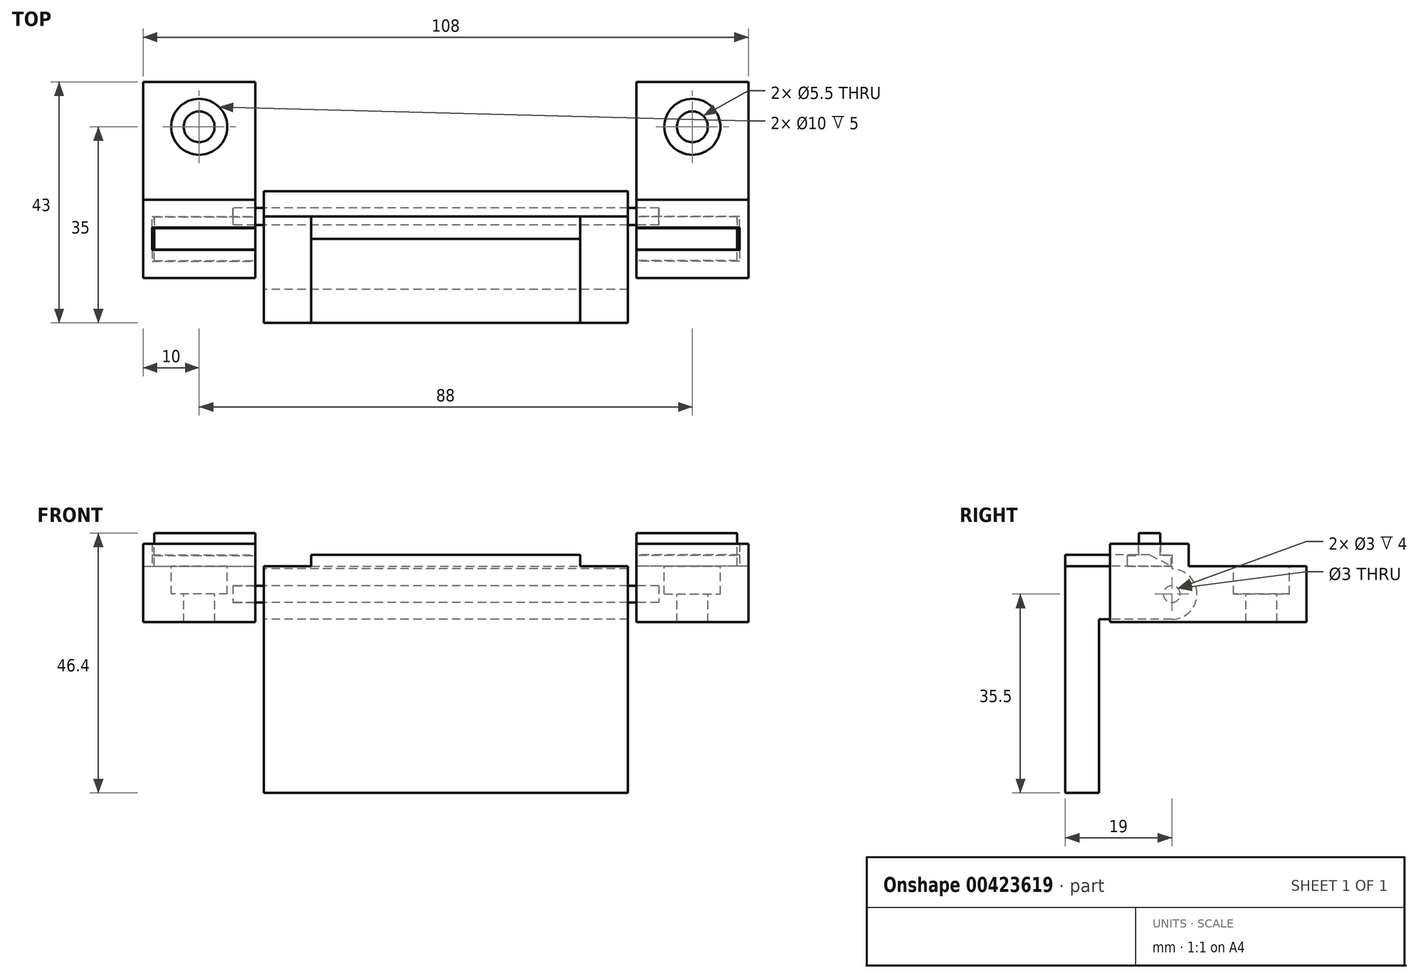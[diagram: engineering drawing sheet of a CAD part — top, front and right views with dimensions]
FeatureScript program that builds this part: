
annotation { "Feature Type Name" : "Feature", "Feature Type Description" : "" }
export const myFeature = defineFeature(function(context is Context, id is Id, definition is map)
    precondition{}
    {
        {
            var Q0;
            Q0=qCreatedBy(makeId("Top.planeOp"),FACE);
            var sketch = newSketch(context, id + "F0", { "sketchPlane" : qUnion([Q0])});
            skLineSegment(sketch, "E0.bottom", {"start": v(-54, 0) * mm, "end": v(-34, 0) * mm});
            skLineSegment(sketch, "E0.top", {"start": v(-54, 35) * mm, "end": v(-34, 35) * mm});
            skLineSegment(sketch, "E0.left", {"start": v(-54, 0) * mm, "end": v(-54, 35) * mm});
            skLineSegment(sketch, "E0.right", {"start": v(-34, 0) * mm, "end": v(-34, 35) * mm});
            skLineSegment(sketch, "E1", {"start": v(-44, 35) * mm, "end": v(-44, 0) * mm, "construction": true});
            skSolve(sketch);
        }
        {
            var Q0;
            Q0=makeQuery(id+"F0.imprint","IMPRINT",FACE,{"disambiguationData":[TD([[makeQuery(id+"F0.imprint","IMPRINT",EDGE,{"derivedFrom":sQuery(id+"F0.wireOp",EDGE,"E0.bottom")}),1.0]])]});
            var Q1;
            Q1=makeQuery(id+"F0.imprint","IMPRINT",FACE,{"disambiguationData":[TD([[makeQuery(id+"F0.imprint","IMPRINT",EDGE,{"derivedFrom":sQuery(id+"F0.wireOp",EDGE,"f8b40c92-a36b-450e-9c67-8d930c3af6210.MirrorCS")}),-1.0]])]});
            extrude(context, id + "F1", {"entities" : qUnion([Q0, Q1]), "depth" : 10 * mm});
        }
        {
            var Q0;
            Q0=makeQuery(id+"F1.opExtrude","CAP_FACE",FACE,{"disambiguationData":[OSD([sQuery(id+"F0.wireOp",EDGE,"E0.bottom"),sQuery(id+"F0.wireOp",EDGE,"E0.top"),sQuery(id+"F0.wireOp",EDGE,"E0.left"),sQuery(id+"F0.wireOp",EDGE,"E0.right")])],"isStart":false});
            var sketch = newSketch(context, id + "F2", { "sketchPlane" : qUnion([Q0])});
            skPoint(sketch, "E2", {"position": v(-44, 27) * mm});
            skLineSegment(sketch, "E3", {"start": v(-44, 35) * mm, "end": v(-44, 0) * mm, "construction": true});
            skLineSegment(sketch, "E4", {"start": v(-54, 17.5) * mm, "end": v(-34, 17.5) * mm, "construction": true});
            skSolve(sketch);
        }
        {
            var Q0;
            Q0=sQuery(id+"F2.wireOp",VERTEX,"E2");
            var Q1;
            Q1=makeQuery(id+"F1.opExtrude","SWEPT_BODY",BODY,{"disambiguationData":[OSD([sQuery(id+"F0.wireOp",EDGE,"E0.bottom"),sQuery(id+"F0.wireOp",EDGE,"E0.top"),sQuery(id+"F0.wireOp",EDGE,"E0.left"),sQuery(id+"F0.wireOp",EDGE,"E0.right")])]});
            hole(context, id + "F3", {"style" : HoleStyle.C_BORE, "endStyle" : HoleEndStyle.THROUGH, "holeDiameter" : 5.5 * mm, "cBoreDiameter" : 10 * mm, "cBoreDepth" : 5 * mm, "isTappedThrough" : true, "tappedDepth" : 3 * mm, "tapClearance" : 3, "locations" : qUnion([Q0]), "scope" : qUnion([Q1])});
        }
        {
            var Q0;
            Q0=makeQuery(id+"F1.opExtrude","SWEPT_FACE",FACE,{"disambiguationData":[OSD([sQuery(id+"F0.wireOp",EDGE,"E0.right")])]});
            var sketch = newSketch(context, id + "F4", { "sketchPlane" : qUnion([Q0])});
            skPoint(sketch, "E5", {"position": v(11, 5) * mm});
            skLineSegment(sketch, "E6", {"start": v(0, 5) * mm, "end": v(35, 5) * mm, "construction": true});
            skCircle(sketch, "E7", {"center": v(11, 5) * mm, "radius": 1.5 * mm});
            skLineSegment(sketch, "E8.0", {"start": v(22, 10) * mm, "end": v(32, 10) * mm, "construction": true});
            skLineSegment(sketch, "E9", {"start": v(22, 10) * mm, "end": v(22, 0) * mm, "construction": true});
            skPoint(sketch, "E10", {"position": v(22, 5) * mm});
            skLineSegment(sketch, "E11", {"start": v(11, 3.5) * mm, "end": v(11, 6.5) * mm, "construction": true});
            skLineSegment(sketch, "E12", {"start": v(0, 10) * mm, "end": v(0, 14) * mm});
            skLineSegment(sketch, "E13", {"start": v(0, 14) * mm, "end": v(5, 14) * mm});
            skLineSegment(sketch, "E14", {"start": v(5, 14) * mm, "end": v(5, 12) * mm});
            skLineSegment(sketch, "E15", {"start": v(5, 12) * mm, "end": v(3, 12) * mm});
            skLineSegment(sketch, "E16", {"start": v(3, 12) * mm, "end": v(3, 10) * mm});
            skLineSegment(sketch, "E17", {"start": v(3, 10) * mm, "end": v(0, 10) * mm});
            skLineSegment(sketch, "E18", {"start": v(7, 10) * mm, "end": v(7, 14) * mm, "construction": true});
            skLineSegment(sketch, "E19.MirrorCS", {"start": v(9, 14) * mm, "end": v(9, 12) * mm});
            skLineSegment(sketch, "E20.MirrorCS", {"start": v(14, 14) * mm, "end": v(9, 14) * mm});
            skLineSegment(sketch, "E21.MirrorCS", {"start": v(14, 10) * mm, "end": v(14, 14) * mm});
            skLineSegment(sketch, "E22.MirrorCS", {"start": v(11, 12) * mm, "end": v(11, 10) * mm});
            skLineSegment(sketch, "E23.MirrorCS", {"start": v(9, 12) * mm, "end": v(11, 12) * mm});
            skLineSegment(sketch, "E24.MirrorCS", {"start": v(11, 10) * mm, "end": v(14, 10) * mm});
            skLineSegment(sketch, "E25", {"start": v(3.1, 10) * mm, "end": v(7, 10) * mm});
            skLineSegment(sketch, "E26", {"start": v(3.1, 10) * mm, "end": v(3.1, 11.9) * mm});
            skLineSegment(sketch, "E27", {"start": v(3.1, 11.9) * mm, "end": v(5.1, 11.9) * mm});
            skLineSegment(sketch, "E28", {"start": v(5.1, 11.9) * mm, "end": v(5.1, 15.9) * mm});
            skLineSegment(sketch, "E29", {"start": v(5.1, 15.9) * mm, "end": v(7, 15.9) * mm});
            skLineSegment(sketch, "E30.MirrorCS", {"start": v(8.9, 15.9) * mm, "end": v(7, 15.9) * mm});
            skLineSegment(sketch, "E31.MirrorCS", {"start": v(8.9, 11.9) * mm, "end": v(8.9, 15.9) * mm});
            skLineSegment(sketch, "E32.MirrorCS", {"start": v(10.9, 10) * mm, "end": v(10.9, 11.9) * mm});
            skLineSegment(sketch, "E33.MirrorCS", {"start": v(10.9, 10) * mm, "end": v(7, 10) * mm});
            skLineSegment(sketch, "E34.MirrorCS", {"start": v(10.9, 11.9) * mm, "end": v(8.9, 11.9) * mm});
            skSolve(sketch);
        }
        {
            var Q0;
            Q0=makeQuery(id+"F4.imprint","IMPRINT",FACE,{"disambiguationData":[TD([[makeQuery(id+"F4.imprint","IMPRINT",EDGE,{"derivedFrom":sQuery(id+"F4.wireOp",EDGE,"E12")}),-1.0]])]});
            var Q1;
            Q1=makeQuery(id+"F4.imprint","IMPRINT",FACE,{"disambiguationData":[TD([[makeQuery(id+"F4.imprint","IMPRINT",EDGE,{"derivedFrom":sQuery(id+"F4.wireOp",EDGE,"E19.MirrorCS")}),1.0]])]});
            var Q2;
            Q2=makeQuery(id+"F1.opExtrude","SWEPT_FACE",FACE,{"disambiguationData":[OSD([sQuery(id+"F0.wireOp",EDGE,"E0.left")])]});
            extrude(context, id + "F5", {"entities" : qUnion([Q0, Q1]), "operationType" : NewBodyOperationType.ADD, "endBound" : BoundingType.UP_TO_SURFACE, "oppositeDirection" : true, "endBoundEntityFace" : qUnion([Q2]), "depth" : 25 * mm});
        }
        {
            var Q0;
            Q0=makeQuery(id+"F4.imprint","IMPRINT",FACE,{"disambiguationData":[TD([[makeQuery(id+"F4.imprint","IMPRINT",EDGE,{"derivedFrom":sQuery(id+"F4.wireOp",EDGE,"E25")}),1.0]])]});
            extrude(context, id + "F6", {"entities" : qUnion([Q0]), "oppositeDirection" : true, "depth" : 18 * mm});
        }
        {
            var Q0;
            {var subQ0=sQuery(id+"F0.wireOp",EDGE,"E0.left");Q0=makeQuery(id+"F5.boolean.opBoolean","MERGE",FACE,{"derivedFrom":[makeQuery(id+"F1.opExtrude","SWEPT_FACE",FACE,{"disambiguationData":[OSD([subQ0])]}),makeQuery(id+"F5.opExtrude","CAP_FACE",FACE,{"disambiguationData":[OSD([subQ0]),ownerDisambiguation([makeQuery(id+"F4.imprint","IMPRINT",EDGE,{"derivedFrom":sQuery(id+"F4.wireOp",EDGE,"E12")})])],"isStart":false}),makeQuery(id+"F5.opExtrude","CAP_FACE",FACE,{"disambiguationData":[OSD([subQ0]),ownerDisambiguation([makeQuery(id+"F4.imprint","IMPRINT",EDGE,{"derivedFrom":sQuery(id+"F4.wireOp",EDGE,"E19.MirrorCS")})])],"isStart":false})]});}
            var sketch = newSketch(context, id + "F7", { "sketchPlane" : qUnion([Q0])});
            skLineSegment(sketch, "E35", {"start": v(-9, 14) * mm, "end": v(-5, 14) * mm});
            skSolve(sketch);
        }
        {
            var Q0;
            Q0 = qSketchRegion(id + "F7", true);
            var Q1;
            Q1=makeQuery(id+"F7.imprint","IMPRINT",FACE,{"disambiguationData":[TD([[makeQuery(id+"F7.imprint","IMPRINT",EDGE,{"derivedFrom":sQuery(id+"F7.wireOp",EDGE,"E35")}),-1.0]])]});
            extrude(context, id + "F8", {"entities" : qUnion([Q0, Q1]), "operationType" : NewBodyOperationType.ADD, "oppositeDirection" : true, "depth" : 1.6 * mm});
        }
        {
            var Q0;
            Q0=makeQuery(id+"F4.imprint","IMPRINT",FACE,{"disambiguationData":[TD([[makeQuery(id+"F4.imprint","IMPRINT",EDGE,{"derivedFrom":sQuery(id+"F4.wireOp",EDGE,"E7")}),1.0]])]});
            extrude(context, id + "F9", {"entities" : qUnion([Q0]), "operationType" : NewBodyOperationType.REMOVE, "oppositeDirection" : true, "depth" : 4 * mm});
        }
        {
            var Q0;
            Q0=makeQuery(id+"F1.opExtrude","SWEPT_BODY",BODY,{"disambiguationData":[OSD([sQuery(id+"F0.wireOp",EDGE,"E0.bottom"),sQuery(id+"F0.wireOp",EDGE,"E0.top"),sQuery(id+"F0.wireOp",EDGE,"E0.left"),sQuery(id+"F0.wireOp",EDGE,"E0.right")])]});
            var Q1;
            Q1=makeQuery(id+"F6.opExtrude","SWEPT_BODY",BODY,{"disambiguationData":[OSD([sQuery(id+"F4.wireOp",EDGE,"E25"),sQuery(id+"F4.wireOp",EDGE,"E26"),sQuery(id+"F4.wireOp",EDGE,"E27"),sQuery(id+"F4.wireOp",EDGE,"E28"),sQuery(id+"F4.wireOp",EDGE,"E29"),sQuery(id+"F4.wireOp",EDGE,"E30.MirrorCS"),sQuery(id+"F4.wireOp",EDGE,"E31.MirrorCS"),sQuery(id+"F4.wireOp",EDGE,"E32.MirrorCS"),sQuery(id+"F4.wireOp",EDGE,"E33.MirrorCS"),sQuery(id+"F4.wireOp",EDGE,"E34.MirrorCS")])]});
            var Q2;
            Q2=qCreatedBy(makeId("Right.planeOp"),FACE);
            mirror(context, id + "F10", {"entities" : qUnion([Q0, Q1]), "mirrorPlane" : qUnion([Q2])});
        }
        {
            var Q0;
            Q0=qCreatedBy(makeId("Right.planeOp"),FACE);
            var sketch = newSketch(context, id + "F11", { "sketchPlane" : qUnion([Q0])});
            skCircle(sketch, "E36.0", {"center": v(11, 5) * mm, "radius": 1.5 * mm});
            skSolve(sketch);
        }
        {
            var Q0;
            Q0 = qSketchRegion(id + "F11", true);
            var Q1;
            Q1=makeQuery(id+"F10.opPattern","COPY",FACE,{"derivedFrom":makeQuery(id+"F9.boolean.opBoolean","COPY",FACE,{"derivedFrom":makeQuery(id+"F9.opExtrude","CAP_FACE",FACE,{"disambiguationData":[OSD([sQuery(id+"F4.wireOp",EDGE,"E7")])],"isStart":false})}),"instanceName":"1"});
            var Q2;
            Q2=makeQuery(id+"F9.boolean.opBoolean","COPY",FACE,{"derivedFrom":makeQuery(id+"F9.opExtrude","CAP_FACE",FACE,{"disambiguationData":[OSD([sQuery(id+"F4.wireOp",EDGE,"E7")])],"isStart":false})});
            extrude(context, id + "F12", {"entities" : qUnion([Q0]), "endBound" : BoundingType.UP_TO_SURFACE, "endBoundEntityFace" : qUnion([Q1]), "depth" : 25 * mm, "hasSecondDirection" : true, "secondDirectionBound" : SecondDirectionBoundingType.UP_TO_SURFACE, "secondDirectionOppositeDirection" : true, "secondDirectionBoundEntityFace" : qUnion([Q2]), "secondDirectionDepth" : 25 * mm});
        }
        {
            var Q0;
            Q0=qCreatedBy(makeId("Right.planeOp"),FACE);
            var sketch = newSketch(context, id + "F13", { "sketchPlane" : qUnion([Q0])});
            skCircle(sketch, "E37.0", {"center": v(11, 5) * mm, "radius": 1.5 * mm, "construction": true});
            skLineSegment(sketch, "E38", {"start": v(11, 0.5) * mm, "end": v(0, 0.5) * mm});
            skLineSegment(sketch, "E39", {"start": v(0, 0.5) * mm, "end": v(-2, 0.5) * mm});
            skLineSegment(sketch, "E40", {"start": v(-2, 0.5) * mm, "end": v(-2, -30.5) * mm});
            skLineSegment(sketch, "E41", {"start": v(-2, -30.5) * mm, "end": v(-8, -30.5) * mm});
            skLineSegment(sketch, "E42", {"start": v(-8, -30.5) * mm, "end": v(-8, 9.5) * mm});
            skLineSegment(sketch, "E43", {"start": v(15.5, 5) * mm, "end": v(-8, 5) * mm, "construction": true});
            skLineSegment(sketch, "E44", {"start": v(11, 9.5) * mm, "end": v(-8, 9.5) * mm});
            skCircle(sketch, "E45", {"center": v(11, 5) * mm, "radius": 4.5 * mm});
            skPoint(sketch, "E46.MirrorCS.start.orphan", {"position": v(15.5, 5) * mm});
            skSolve(sketch);
        }
        {
            var Q0;
            Q0=makeQuery(id+"F13.imprint","IMPRINT",FACE,{"disambiguationData":[TD([[makeQuery(id+"F13.imprint","IMPRINT",EDGE,{"derivedFrom":sQuery(id+"F13.wireOp",EDGE,"smrf8rLL-LFyA-yOWK-lnng-tCgB0Rm7KVjo")}),-1.0]])]});
            var Q1;
            Q1=makeQuery(id+"F13.imprint","IMPRINT",FACE,{"disambiguationData":[TD([[makeQuery(id+"F13.imprint","IMPRINT",EDGE,{"derivedFrom":sQuery(id+"F13.wireOp",EDGE,"KXUtPn0d-eV9m-ZpY6-MxWF-lvJaAZIAgiPy")}),-1.0]])]});
            var Q2;
            {var subQ0=sQuery(id+"F13.wireOp",EDGE,"E38");Q2=makeQuery(id+"F13.imprint","IMPRINT",FACE,{"disambiguationData":[TD([[makeQuery(id+"F13.imprint","IMPRINT",EDGE,{"derivedFrom":subQ0}),-1.0]])]});}
            var Q3;
            {var subQ0=sQuery(id+"F13.wireOp",EDGE,"E45");var subQ1=makeQuery(id+"F13.imprint","INTERSECT",VERTEX,{"derivedFrom":[sQuery(id+"F13.wireOp",EDGE,"E38"),subQ0]});Q3=makeQuery(id+"F13.imprint","IMPRINT",FACE,{"disambiguationData":[TD([[makeQuery(id+"F13.imprint","IMPRINT",EDGE,{"disambiguationData":[TD([[subQ1,1.0]])],"derivedFrom":subQ0}),1.0]])]});}
            extrude(context, id + "F14", {"entities" : qUnion([Q0, Q1, Q2, Q3]), "endBound" : BoundingType.SYMMETRIC, "depth" : 65 * mm});
        }
        {
            var Q0;
            Q0=makeQuery(id+"F12.opExtrude","SWEPT_BODY",BODY,{"disambiguationData":[OSD([sQuery(id+"F11.wireOp",EDGE,"E36.0")])]});
            var Q1;
            Q1=makeQuery(id+"F14.opExtrude","SWEPT_BODY",BODY,{"disambiguationData":[OSD([sQuery(id+"F13.wireOp",EDGE,"smrf8rLL-LFyA-yOWK-lnng-tCgB0Rm7KVjo"),sQuery(id+"F13.wireOp",EDGE,"KXUtPn0d-eV9m-ZpY6-MxWF-lvJaAZIAgiPy"),sQuery(id+"F13.wireOp",EDGE,"145327e7-5e28-42c3-9492-394448290486"),sQuery(id+"F13.wireOp",EDGE,"E38"),sQuery(id+"F13.wireOp",EDGE,"E39"),sQuery(id+"F13.wireOp",EDGE,"E40"),sQuery(id+"F13.wireOp",EDGE,"E41"),sQuery(id+"F13.wireOp",EDGE,"E42")])]});
            booleanBodies(context, id + "F15", {"operationType" : BooleanOperationType.SUBTRACTION, "tools" : qUnion([Q0]), "targets" : qUnion([Q1]), "keepTools" : true});
        }
        {
            var Q0;
            Q0=makeQuery(id+"F14.opExtrude","SWEPT_FACE",FACE,{"disambiguationData":[OSD([sQuery(id+"F13.wireOp",EDGE,"E44")])]});
            var sketch = newSketch(context, id + "F16", { "sketchPlane" : qUnion([Q0])});
            skLineSegment(sketch, "E47.bottom", {"start": v(-32.5, 11) * mm, "end": v(32.5, 11) * mm});
            skLineSegment(sketch, "E47.top", {"start": v(-32.5, -8) * mm, "end": v(32.5, -8) * mm});
            skLineSegment(sketch, "E47.left", {"start": v(-32.5, 11) * mm, "end": v(-32.5, -8) * mm});
            skLineSegment(sketch, "E47.right", {"start": v(32.5, 11) * mm, "end": v(32.5, -8) * mm});
            skSolve(sketch);
        }
        {
            var Q0;
            Q0=makeQuery(id+"F16.imprint","IMPRINT",FACE,{"disambiguationData":[TD([[makeQuery(id+"F16.imprint","IMPRINT",EDGE,{"derivedFrom":sQuery(id+"F16.wireOp",EDGE,"E47.bottom")}),1.0]])]});
            var Q1;
            Q1=makeQuery(id+"F1.opExtrude","CAP_FACE",FACE,{"disambiguationData":[OSD([sQuery(id+"F0.wireOp",EDGE,"E0.bottom"),sQuery(id+"F0.wireOp",EDGE,"E0.top"),sQuery(id+"F0.wireOp",EDGE,"E0.left"),sQuery(id+"F0.wireOp",EDGE,"E0.right")])],"isStart":false});
            extrude(context, id + "F17", {"entities" : qUnion([Q0]), "operationType" : NewBodyOperationType.ADD, "endBound" : BoundingType.UP_TO_SURFACE, "endBoundEntityFace" : qUnion([Q1]), "depth" : 25 * mm});
        }
        {
            var Q0;
            Q0=makeQuery(id+"F17.opExtrude","CAP_FACE",FACE,{"disambiguationData":[OSD([sQuery(id+"F16.wireOp",EDGE,"E47.bottom"),sQuery(id+"F16.wireOp",EDGE,"E47.top"),sQuery(id+"F16.wireOp",EDGE,"E47.left"),sQuery(id+"F16.wireOp",EDGE,"E47.right")])],"isStart":false});
            var sketch = newSketch(context, id + "F18", { "sketchPlane" : qUnion([Q0])});
            skLineSegment(sketch, "E48.bottom", {"start": v(-24, 11) * mm, "end": v(24, 11) * mm});
            skLineSegment(sketch, "E48.top", {"start": v(-24, -8) * mm, "end": v(24, -8) * mm});
            skLineSegment(sketch, "E48.left", {"start": v(-24, 11) * mm, "end": v(-24, -8) * mm});
            skLineSegment(sketch, "E48.right", {"start": v(24, 11) * mm, "end": v(24, -8) * mm});
            skSolve(sketch);
        }
        {
            var Q0;
            Q0=makeQuery(id+"F18.imprint","IMPRINT",FACE,{"disambiguationData":[TD([[makeQuery(id+"F18.imprint","IMPRINT",EDGE,{"derivedFrom":sQuery(id+"F18.wireOp",EDGE,"E48.bottom")}),1.0]])]});
            extrude(context, id + "F19", {"entities" : qUnion([Q0]), "operationType" : NewBodyOperationType.ADD, "depth" : 2 * mm});
        }
        {
            var Q0;
            Q0=makeQuery(id+"F19.opExtrude","CAP_EDGE",EDGE,{"disambiguationData":[OSD([sQuery(id+"F18.wireOp",EDGE,"E48.bottom")])],"isStart":false});
            chamfer(context, id + "F20", {"entities" : qUnion([Q0]), "chamferType" : ChamferType.TWO_OFFSETS, "width1" : 4 * mm, "oppositeDirection" : false, "width2" : 2 * mm, "tangentPropagation" : true});
        }
    });
